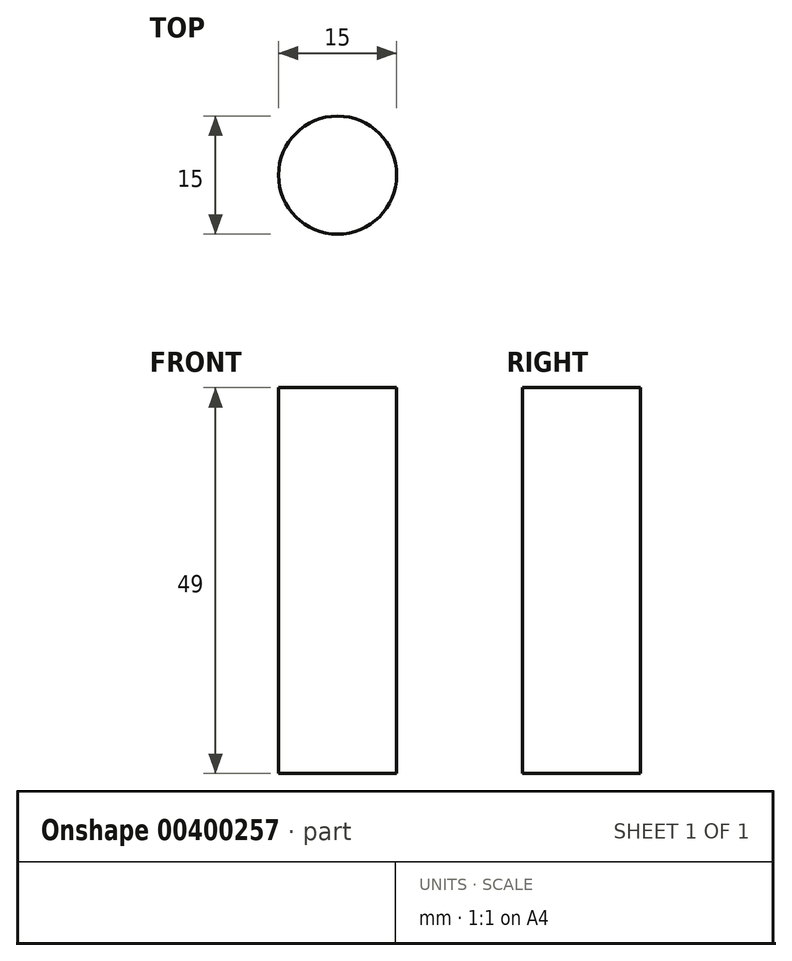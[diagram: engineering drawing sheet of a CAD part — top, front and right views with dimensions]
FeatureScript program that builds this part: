
annotation { "Feature Type Name" : "Feature", "Feature Type Description" : "" }
export const myFeature = defineFeature(function(context is Context, id is Id, definition is map)
    precondition{}
    {
        {
            var Q0;
            Q0=qCreatedBy(makeId("Top.planeOp"),FACE);
            var sketch = newSketch(context, id + "F0", { "sketchPlane" : qUnion([Q0])});
            skCircle(sketch, "E0", {"center": v(0, 0) * mm, "radius": 7.5 * mm});
            skSolve(sketch);
        }
        {
            var Q0;
            Q0 = qSketchRegion(id + "F0", true);
            extrude(context, id + "F1", {"entities" : qUnion([Q0]), "depth" : 49 * mm});
        }
    });
